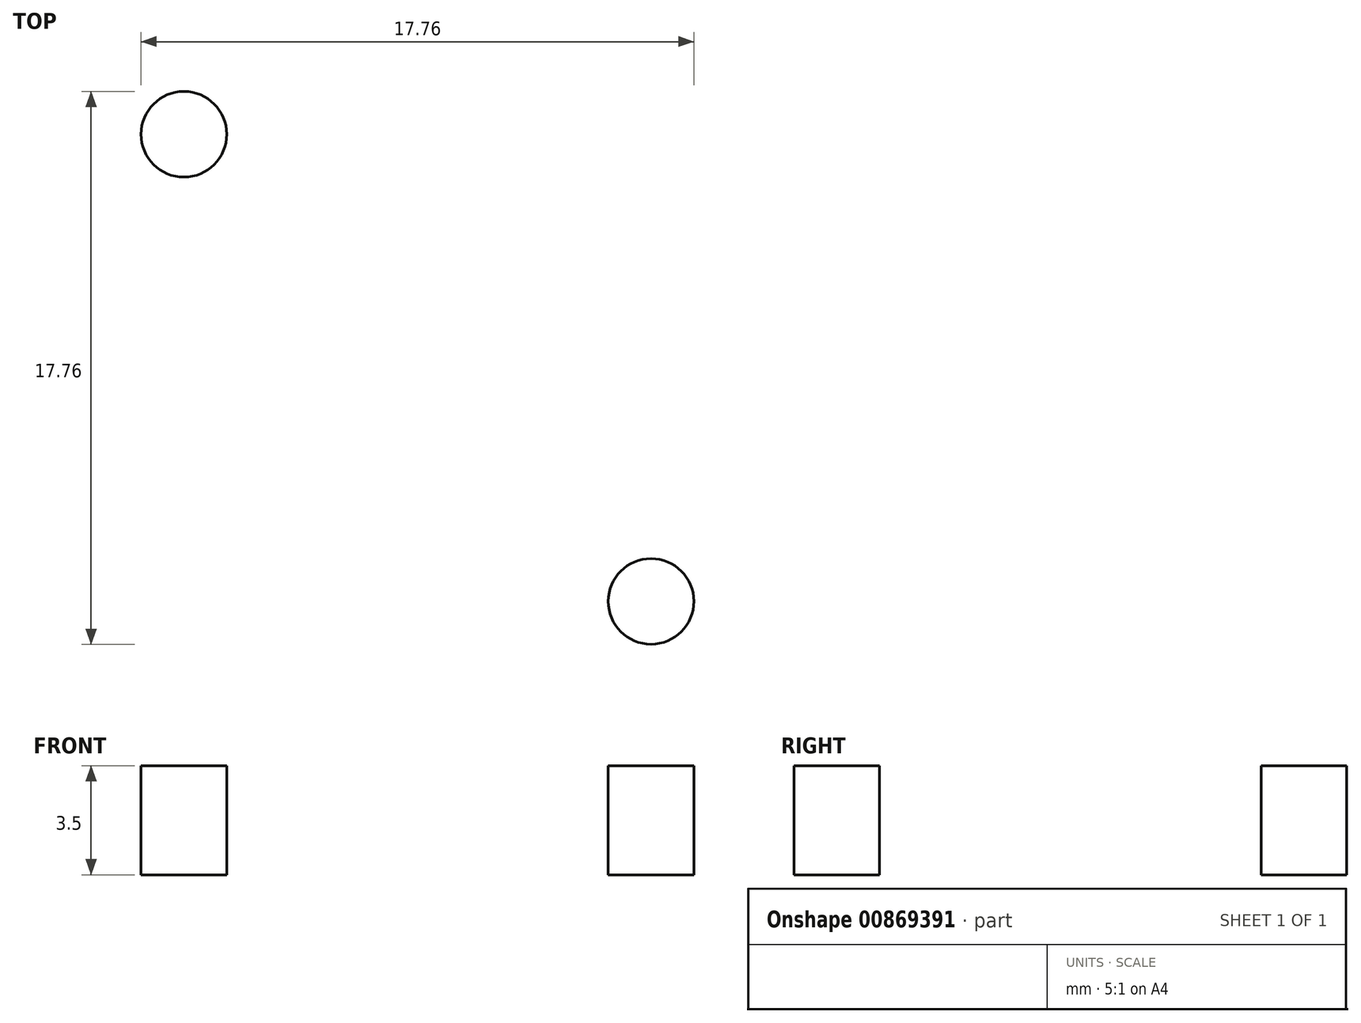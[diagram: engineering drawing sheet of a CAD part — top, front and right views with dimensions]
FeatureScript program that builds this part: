
annotation { "Feature Type Name" : "Feature", "Feature Type Description" : "" }
export const myFeature = defineFeature(function(context is Context, id is Id, definition is map)
    precondition{}
    {
        {
            var Q0;
            Q0=qCreatedBy(makeId("Top.planeOp"),FACE);
            var sketch = newSketch(context, id + "F0", { "sketchPlane" : qUnion([Q0])});
            skLineSegment(sketch, "E0.bottom", {"start": v(0, 0) * mm, "end": v(20, 0) * mm});
            skLineSegment(sketch, "E0.top", {"start": v(0, 20) * mm, "end": v(20, 20) * mm});
            skLineSegment(sketch, "E0.left", {"start": v(0, 0) * mm, "end": v(0, 20) * mm});
            skLineSegment(sketch, "E0.right", {"start": v(20, 0) * mm, "end": v(20, 20) * mm});
            skSolve(sketch);
        }
        {
            var Q0;
            Q0=makeQuery(id+"F0.imprint","IMPRINT",FACE,{"disambiguationData":[TD([[makeQuery(id+"F0.imprint","IMPRINT",EDGE,{"derivedFrom":sQuery(id+"F0.wireOp",EDGE,"E0.bottom")}),1.0]])]});
            extrude(context, id + "F1", {"entities" : qUnion([Q0]), "depth" : 5 * mm, "offsetDistance" : 25 * mm});
        }
        {
            var Q0;
            Q0=makeQuery(id+"F1.opExtrude","CAP_FACE",FACE,{"disambiguationData":[OSD([sQuery(id+"F0.wireOp",EDGE,"E0.bottom"),sQuery(id+"F0.wireOp",EDGE,"E0.top"),sQuery(id+"F0.wireOp",EDGE,"E0.left"),sQuery(id+"F0.wireOp",EDGE,"E0.right")])],"isStart":false});
            var sketch = newSketch(context, id + "F2", { "sketchPlane" : qUnion([Q0])});
            skCircle(sketch, "E1", {"center": v(10, 10) * mm, "radius": 3 * mm});
            skPoint(sketch, "E1.centerSnap0", {"position": v(10, 0) * mm});
            skPoint(sketch, "E1.centerSnap1", {"position": v(0, 10) * mm});
            skLineSegment(sketch, "E2", {"start": v(0, 10) * mm, "end": v(20, 10) * mm, "construction": true});
            skLineSegment(sketch, "E3", {"start": v(10, 20) * mm, "end": v(10, 0) * mm, "construction": true});
            skCircle(sketch, "E4", {"center": v(2.5, 2.5) * mm, "radius": 1.38 * mm});
            skCircle(sketch, "E5.MirrorC", {"center": v(2.5, 17.5) * mm, "radius": 1.38 * mm});
            skCircle(sketch, "E6.MirrorC", {"center": v(17.5, 17.5) * mm, "radius": 1.38 * mm});
            skCircle(sketch, "E7.MirrorC", {"center": v(17.5, 2.5) * mm, "radius": 1.38 * mm});
            skSolve(sketch);
        }
        {
            var Q0;
            Q0=makeQuery(id+"F2.imprint","IMPRINT",FACE,{"disambiguationData":[TD([[makeQuery(id+"F2.imprint","IMPRINT",EDGE,{"derivedFrom":sQuery(id+"F2.wireOp",EDGE,"E1")}),1.0]])]});
            var Q1;
            Q1=makeQuery(id+"F2.imprint","IMPRINT",FACE,{"disambiguationData":[TD([[makeQuery(id+"F2.imprint","IMPRINT",EDGE,{"derivedFrom":sQuery(id+"F2.wireOp",EDGE,"E5.MirrorC")}),-1.0]])]});
            var Q2;
            Q2=makeQuery(id+"F2.imprint","IMPRINT",FACE,{"disambiguationData":[TD([[makeQuery(id+"F2.imprint","IMPRINT",EDGE,{"derivedFrom":sQuery(id+"F2.wireOp",EDGE,"E6.MirrorC")}),1.0]])]});
            var Q3;
            Q3=makeQuery(id+"F2.imprint","IMPRINT",FACE,{"disambiguationData":[TD([[makeQuery(id+"F2.imprint","IMPRINT",EDGE,{"derivedFrom":sQuery(id+"F2.wireOp",EDGE,"E7.MirrorC")}),-1.0]])]});
            var Q4;
            Q4=makeQuery(id+"F2.imprint","IMPRINT",FACE,{"disambiguationData":[TD([[makeQuery(id+"F2.imprint","IMPRINT",EDGE,{"derivedFrom":sQuery(id+"F2.wireOp",EDGE,"E4")}),1.0]])]});
            extrude(context, id + "F3", {"entities" : qUnion([Q0, Q1, Q2, Q3, Q4]), "operationType" : NewBodyOperationType.REMOVE, "oppositeDirection" : true, "depth" : 25 * mm, "offsetDistance" : 25 * mm});
        }
        {
            var Q0;
            Q0=makeQuery(id+"F1.opExtrude","CAP_FACE",FACE,{"disambiguationData":[OSD([sQuery(id+"F0.wireOp",EDGE,"E0.bottom"),sQuery(id+"F0.wireOp",EDGE,"E0.top"),sQuery(id+"F0.wireOp",EDGE,"E0.left"),sQuery(id+"F0.wireOp",EDGE,"E0.right")])],"isStart":false});
            var sketch = newSketch(context, id + "F4", { "sketchPlane" : qUnion([Q0])});
            skCircle(sketch, "E8", {"center": v(10, 10) * mm, "radius": 5 * mm});
            skSolve(sketch);
        }
        {
            var Q0;
            Q0=makeQuery(id+"F4.imprint","IMPRINT",FACE,{"disambiguationData":[TD([[makeQuery(id+"F4.imprint","IMPRINT",EDGE,{"derivedFrom":sQuery(id+"F4.wireOp",EDGE,"E8")}),1.0]])]});
            extrude(context, id + "F5", {"entities" : qUnion([Q0]), "operationType" : NewBodyOperationType.REMOVE, "oppositeDirection" : true, "depth" : 3.5 * mm, "offsetDistance" : 25 * mm});
        }
        {
            var Q0;
            Q0=makeQuery(id+"F1.opExtrude","CAP_FACE",FACE,{"disambiguationData":[OSD([sQuery(id+"F0.wireOp",EDGE,"E0.bottom"),sQuery(id+"F0.wireOp",EDGE,"E0.top"),sQuery(id+"F0.wireOp",EDGE,"E0.left"),sQuery(id+"F0.wireOp",EDGE,"E0.right")])],"isStart":false});
            var sketch = newSketch(context, id + "F6", { "sketchPlane" : qUnion([Q0])});
            skCircle(sketch, "E9", {"center": v(10, 10) * mm, "radius": 7.5 * mm});
            skSolve(sketch);
        }
        {
            var Q0;
            Q0=makeQuery(id+"F6.imprint","IMPRINT",FACE,{"disambiguationData":[TD([[makeQuery(id+"F6.imprint","IMPRINT",EDGE,{"derivedFrom":sQuery(id+"F6.wireOp",EDGE,"E9")}),1.0]])]});
            var Q1;
            Q1=qSketchRegion(id+"F2",true);
            extrude(context, id + "F7", {"entities" : qUnion([Q0, Q1]), "operationType" : NewBodyOperationType.REMOVE, "oppositeDirection" : true, "depth" : 1.5 * mm, "offsetDistance" : 25 * mm});
        }
    });
